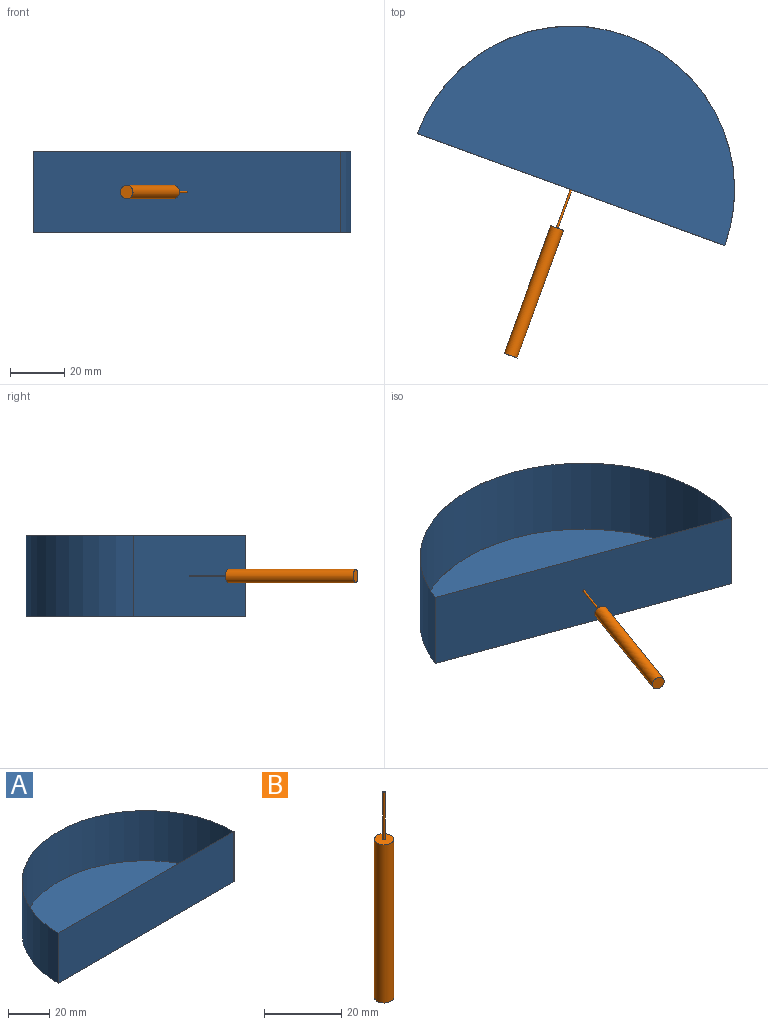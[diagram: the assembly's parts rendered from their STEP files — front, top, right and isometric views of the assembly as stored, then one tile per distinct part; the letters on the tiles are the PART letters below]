
ASSEMBLY  parts=2 mates=1
PART A: 7 faces, bbox 120.4x60.2x29.7 mm
  f0: cylinder r=60.2mm len=120.39mm, axis (0,0,-1), area 5622.2mm2, adj f1,f2,f3
  f1: plane 120.39x29.73mm, normal (0,-1,0), area 3579.2mm2, adj f0,f2,f3
  f2: plane 120.39x60.2mm, normal (0,0,1), area 7.9mm2, adj f0,f1,f4,f5
  f3: plane 120.39x60.2mm, normal (0,0,-1), area 5691.7mm2, adj f0,f1
  f4: cylinder r=60.17mm len=120.34mm, axis (0,0,-1), area 5613.5mm2, adj f2,f5,f6
  f5: plane 120.34x29.7mm, normal (0,1,0), area 3574.6mm2, adj f2,f4,f6
  f6: plane 120.34x60.14mm, normal (0,0,1), area 5683.8mm2, adj f4,f5
PART B: 5 faces, bbox 5x5x65 mm
  f0: cylinder r=2.5mm len=50mm, axis (0,0,-1), area 785.4mm2, adj f1,f2
  f1: plane 5x5mm, normal (0,0,1), area 19.3mm2, adj f0,f3
  f2: plane 5x5mm, normal (0,0,-1), area 19.6mm2, adj f0
  f3: cylinder r=0.35mm len=15mm, axis (0,0,-1), area 33mm2, adj f1,f4
  f4: plane 0.7x0.7mm, normal (0,0,1), area 0.4mm2, adj f3
PLACE A rot(axis=(0,0,-1),20deg) t=(-10.29,1.82,-11.18)mm
PLACE B rot(axis=(-0.97,0.17,-0.17),91.7deg) t=(-32.53,-59.26,3.69)mm
MATE planar B.f3 <-> A.f1  axis (0.34,0.94,0) through (-10.29,1.82,3.69)mm
